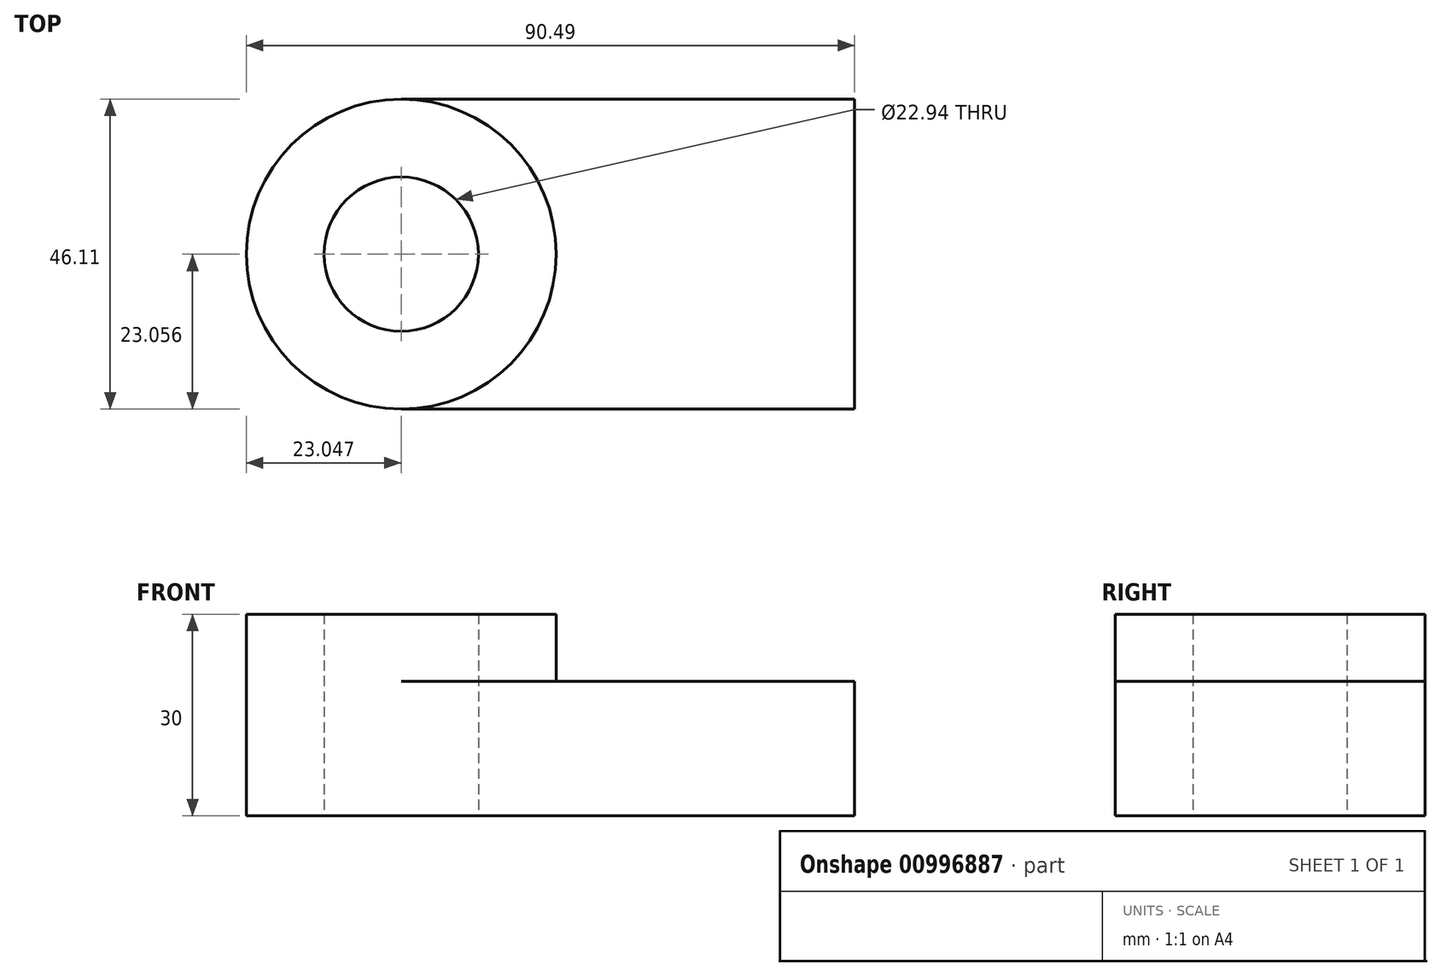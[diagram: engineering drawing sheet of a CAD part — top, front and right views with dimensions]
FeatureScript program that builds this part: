
annotation { "Feature Type Name" : "Feature", "Feature Type Description" : "" }
export const myFeature = defineFeature(function(context is Context, id is Id, definition is map)
    precondition{}
    {
        {
            var Q0;
            Q0=qCreatedBy(makeId("Top.planeOp"),FACE);
            var sketch = newSketch(context, id + "F0", { "sketchPlane" : qUnion([Q0])});
            skLineSegment(sketch, "E0.bottom", {"start": v(-41.12, 29.6) * mm, "end": v(26.32, 29.6) * mm});
            skLineSegment(sketch, "E0.top", {"start": v(-41.12, -16.5) * mm, "end": v(26.32, -16.5) * mm});
            skLineSegment(sketch, "E0.left", {"start": v(-41.12, 29.6) * mm, "end": v(-41.12, -16.5) * mm});
            skLineSegment(sketch, "E0.right", {"start": v(26.32, 29.6) * mm, "end": v(26.32, -16.5) * mm});
            skCircle(sketch, "E1", {"center": v(-41.12, 6.55) * mm, "radius": 23.05 * mm});
            skCircle(sketch, "E2", {"center": v(-41.12, 6.55) * mm, "radius": 11.47 * mm});
            skSolve(sketch);
        }
        {
            var Q0;
            Q0 = qSketchRegion(id + "F0", true);
            extrude(context, id + "F1", {"entities" : qUnion([Q0]), "depth" : 20 * mm, "offsetDistance" : 25.4 * mm});
        }
        {
            var Q0;
            {var subQ1=sQuery(id+"F0.wireOp",EDGE,"E0.left");var subQ3=sQuery(id+"F0.wireOp",EDGE,"E2");var subQ4=makeQuery(id+"F0.imprint","INTERSECT",VERTEX,{"disambiguationData":[OD(0.0)],"derivedFrom":[subQ1,subQ3]});Q0=makeQuery(id+"F0.imprint","IMPRINT",FACE,{"disambiguationData":[TD([[makeQuery(id+"F0.imprint","IMPRINT",EDGE,{"disambiguationData":[TD([[subQ4,1.0]])],"derivedFrom":subQ3}),-1.0]])]});}
            var Q1;
            {var subQ1=sQuery(id+"F0.wireOp",EDGE,"E0.left");var subQ3=sQuery(id+"F0.wireOp",EDGE,"E2");var subQ4=makeQuery(id+"F0.imprint","INTERSECT",VERTEX,{"disambiguationData":[OD(0.0)],"derivedFrom":[subQ1,subQ3]});Q1=makeQuery(id+"F0.imprint","IMPRINT",FACE,{"disambiguationData":[TD([[makeQuery(id+"F0.imprint","IMPRINT",EDGE,{"disambiguationData":[TD([[subQ4,-1.0]])],"derivedFrom":subQ3}),-1.0]])]});}
            extrude(context, id + "F2", {"entities" : qUnion([Q0, Q1]), "operationType" : NewBodyOperationType.ADD, "depth" : 30 * mm, "offsetDistance" : 25.4 * mm});
        }
    });
